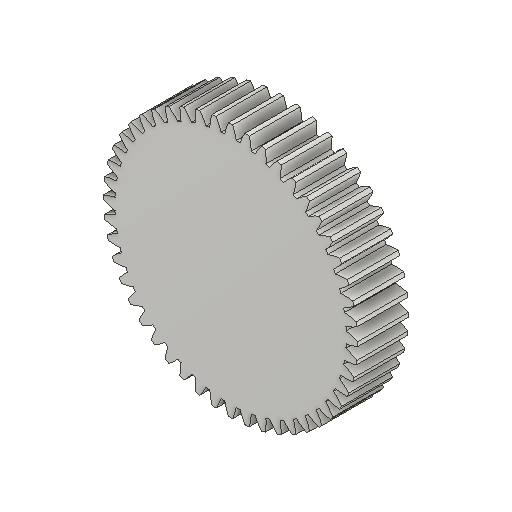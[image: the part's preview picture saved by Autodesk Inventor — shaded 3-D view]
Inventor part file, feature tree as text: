
AUTODESK INVENTOR PART (.ipt)
format: ipt  version: 2024 (Build 280153000, 153)  size: 334,848 bytes
history: native  units: mm (DEFAULTED — no unit token found)
features: plane x3, other x3, extrude x1, sketch x1
ambient origin geometry x8: Origin, YZ Plane, XZ Plane, XY Plane, X Axis, Y Axis, Z Axis, Center Point
bodies: Solid1 (feature_tree)
feature tree (8):
  extrude  "Extrusion1"  Depth=20.0mm TaperAngle=0.0deg
  plane  "Work Plane2"
  plane  "Work Plane8"
  plane  "Work Plane9"
  other  "Spur Gear"
  sketch  "Sketch1"  dims[d0=100.0mm d1=20.0mm d2=0.0mm d3=96.0mm d4=10.0mm d5=0.0mm d16=60.0mm d17=0.0mm d34=0.654498mm d39=0.0mm d41=0.0mm d43=60.0mm d46=60.0mm d47=0.0mm d48=0.0mm]
  other  "Srf1"
  other  "Pitch Diameter"
